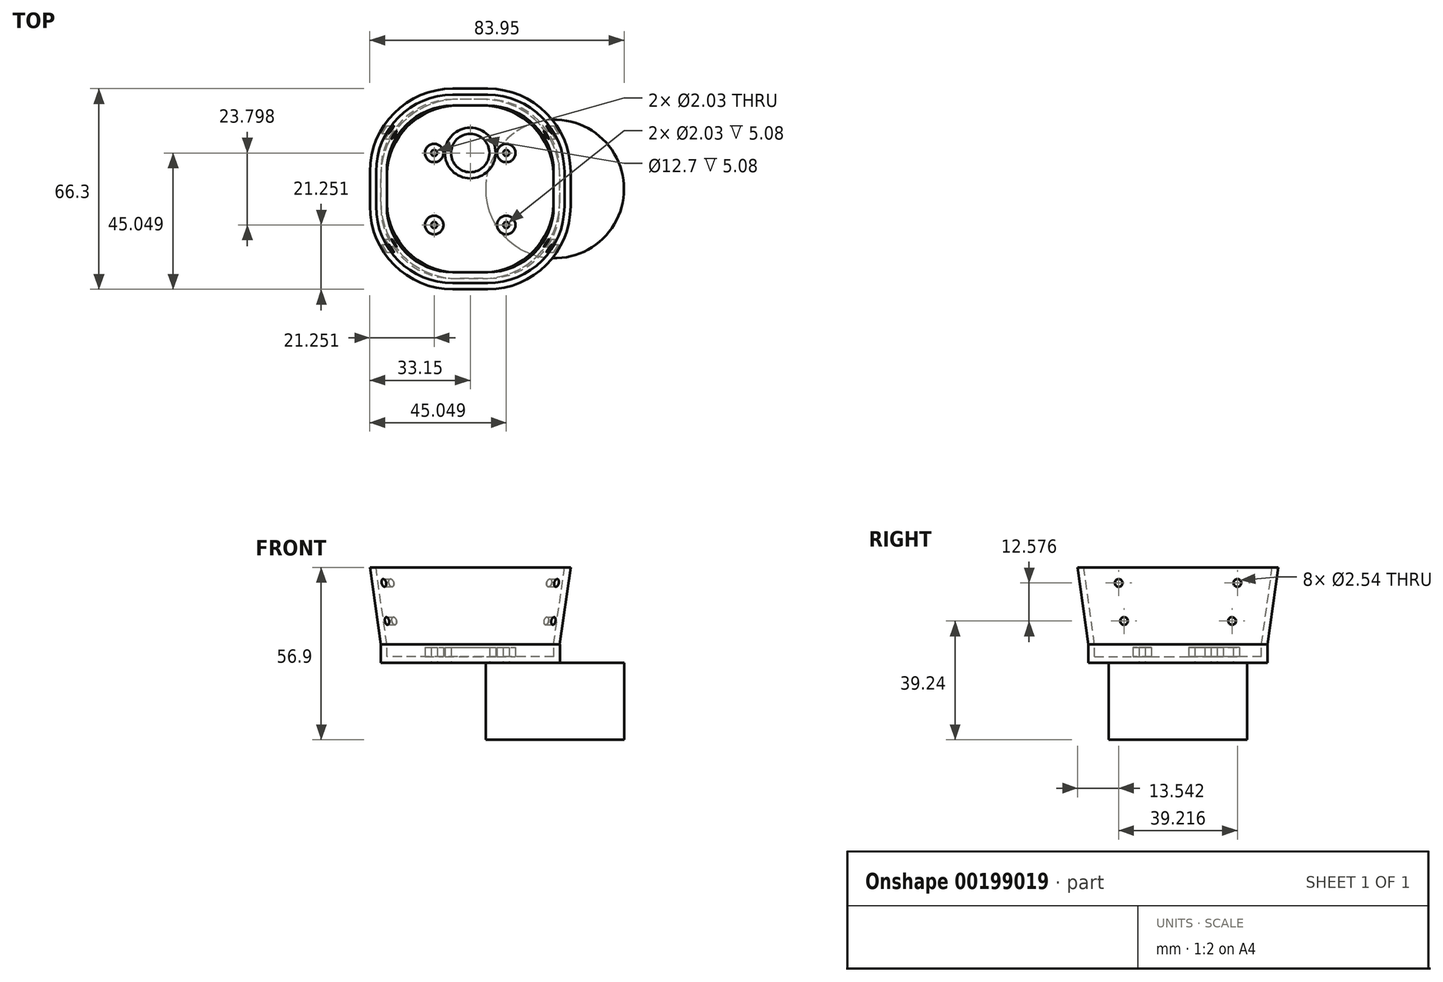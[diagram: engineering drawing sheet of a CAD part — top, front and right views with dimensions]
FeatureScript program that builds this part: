
annotation { "Feature Type Name" : "Feature", "Feature Type Description" : "" }
export const myFeature = defineFeature(function(context is Context, id is Id, definition is map)
    precondition{}
    {
        {
            var Q0;
            Q0=qCreatedBy(makeId("Top.planeOp"),FACE);
            var sketch = newSketch(context, id + "F0", { "sketchPlane" : qUnion([Q0])});
            skLineSegment(sketch, "E0.bottom", {"start": v(29.6, -29.6) * mm, "end": v(-29.6, -29.6) * mm});
            skLineSegment(sketch, "E0.top", {"start": v(29.6, 29.6) * mm, "end": v(-29.6, 29.6) * mm});
            skLineSegment(sketch, "E0.left", {"start": v(29.6, -29.6) * mm, "end": v(29.6, 29.6) * mm});
            skLineSegment(sketch, "E0.right", {"start": v(-29.6, -29.6) * mm, "end": v(-29.6, 29.6) * mm});
            skPoint(sketch, "E0.middle", {"position": v(0, 0) * mm});
            skSolve(sketch);
        }
        {
            var Q0;
            Q0 = qSketchRegion(id + "F0", true);
            extrude(context, id + "F1", {"entities" : qUnion([Q0]), "depth" : 1.02 * mm});
        }
        {
            var Q0;
            Q0=makeQuery(id+"F1.opExtrude","SWEPT_EDGE",EDGE,{"disambiguationData":[OSD([sQuery(id+"F0.wireOp",EDGE,"E0.top"),sQuery(id+"F0.wireOp",EDGE,"E0.right")])]});
            var Q1;
            Q1=makeQuery(id+"F1.opExtrude","SWEPT_EDGE",EDGE,{"disambiguationData":[OSD([sQuery(id+"F0.wireOp",EDGE,"E0.bottom"),sQuery(id+"F0.wireOp",EDGE,"E0.right")])]});
            var Q2;
            Q2=makeQuery(id+"F1.opExtrude","SWEPT_EDGE",EDGE,{"disambiguationData":[OSD([sQuery(id+"F0.wireOp",EDGE,"E0.bottom"),sQuery(id+"F0.wireOp",EDGE,"E0.left")])]});
            var Q3;
            Q3=makeQuery(id+"F1.opExtrude","SWEPT_EDGE",EDGE,{"disambiguationData":[OSD([sQuery(id+"F0.wireOp",EDGE,"E0.top"),sQuery(id+"F0.wireOp",EDGE,"E0.left")])]});
            fillet(context, id + "F2", {"entities" : qUnion([Q0, Q1, Q2, Q3]), "radius" : 25.4 * mm, "tangentPropagation" : true, "allowEdgeOverflow" : false});
        }
        {
            var Q0;
            Q0=makeQuery(id+"F1.opExtrude","CAP_FACE",FACE,{"disambiguationData":[OSD([sQuery(id+"F0.wireOp",EDGE,"E0.bottom"),sQuery(id+"F0.wireOp",EDGE,"E0.top"),sQuery(id+"F0.wireOp",EDGE,"E0.left"),sQuery(id+"F0.wireOp",EDGE,"E0.right")])],"isStart":false});
            var sketch = newSketch(context, id + "F3", { "sketchPlane" : qUnion([Q0])});
            skArc(sketch, "E1.0", {"start": v(-27.56, -4.2) * mm, "mid": v(-20.71, -20.71) * mm, "end": v(-4.2, -27.56) * mm});
            skLineSegment(sketch, "E1.1", {"start": v(-27.56, 4.2) * mm, "end": v(-27.56, -4.2) * mm});
            skLineSegment(sketch, "E1.2", {"start": v(-4.2, -27.56) * mm, "end": v(4.2, -27.56) * mm});
            skArc(sketch, "E1.3", {"start": v(-4.2, 27.56) * mm, "mid": v(-20.71, 20.71) * mm, "end": v(-27.56, 4.2) * mm});
            skArc(sketch, "E1.4", {"start": v(4.2, -27.56) * mm, "mid": v(20.71, -20.71) * mm, "end": v(27.56, -4.2) * mm});
            skLineSegment(sketch, "E1.5", {"start": v(27.56, -4.2) * mm, "end": v(27.56, 4.2) * mm});
            skArc(sketch, "E1.6", {"start": v(27.56, 4.2) * mm, "mid": v(20.71, 20.71) * mm, "end": v(4.2, 27.56) * mm});
            skLineSegment(sketch, "E1.7", {"start": v(4.2, 27.56) * mm, "end": v(-4.2, 27.56) * mm});
            skSolve(sketch);
        }
        {
            var Q0;
            Q0 = qSketchRegion(id + "F3", true);
            extrude(context, id + "F4", {"entities" : qUnion([Q0]), "operationType" : NewBodyOperationType.REMOVE, "oppositeDirection" : true, "depth" : 25.4 * mm});
        }
        {
            var Q0;
            Q0=makeQuery(id+"F1.opExtrude","CAP_FACE",FACE,{"disambiguationData":[OSD([sQuery(id+"F0.wireOp",EDGE,"E0.bottom"),sQuery(id+"F0.wireOp",EDGE,"E0.top"),sQuery(id+"F0.wireOp",EDGE,"E0.left"),sQuery(id+"F0.wireOp",EDGE,"E0.right")])],"isStart":true});
            var sketch = newSketch(context, id + "F5", { "sketchPlane" : qUnion([Q0])});
            skArc(sketch, "E2.0", {"start": v(-4.2, 29.6) * mm, "mid": v(-22.15, 22.15) * mm, "end": v(-29.6, 4.2) * mm});
            skLineSegment(sketch, "E2.1", {"start": v(4.2, 29.6) * mm, "end": v(-4.2, 29.6) * mm});
            skArc(sketch, "E2.2", {"start": v(29.6, 4.2) * mm, "mid": v(22.15, 22.15) * mm, "end": v(4.2, 29.6) * mm});
            skLineSegment(sketch, "E2.3", {"start": v(29.6, 4.2) * mm, "end": v(29.6, -4.2) * mm});
            skLineSegment(sketch, "E2.4", {"start": v(-29.6, 4.2) * mm, "end": v(-29.6, -4.2) * mm});
            skArc(sketch, "E2.5", {"start": v(-29.6, -4.2) * mm, "mid": v(-22.15, -22.15) * mm, "end": v(-4.2, -29.6) * mm});
            skLineSegment(sketch, "E2.6", {"start": v(4.2, -29.6) * mm, "end": v(-4.2, -29.6) * mm});
            skArc(sketch, "E2.7", {"start": v(4.2, -29.6) * mm, "mid": v(22.15, -22.15) * mm, "end": v(29.6, -4.2) * mm});
            skSolve(sketch);
        }
        {
            var Q0;
            Q0 = qSketchRegion(id + "F5", true);
            extrude(context, id + "F6", {"entities" : qUnion([Q0]), "operationType" : NewBodyOperationType.ADD, "depth" : 5.08 * mm});
        }
        {
            var Q0;
            Q0=makeQuery(id+"F6.opExtrude","CAP_FACE",FACE,{"disambiguationData":[OSD([sQuery(id+"F5.wireOp",EDGE,"E2.0"),sQuery(id+"F5.wireOp",EDGE,"E2.1"),sQuery(id+"F5.wireOp",EDGE,"E2.2"),sQuery(id+"F5.wireOp",EDGE,"E2.3"),sQuery(id+"F5.wireOp",EDGE,"E2.4"),sQuery(id+"F5.wireOp",EDGE,"E2.5"),sQuery(id+"F5.wireOp",EDGE,"E2.6"),sQuery(id+"F5.wireOp",EDGE,"E2.7")])],"isStart":false});
            var sketch = newSketch(context, id + "F7", { "sketchPlane" : qUnion([Q0])});
            skLineSegment(sketch, "E3", {"start": v(0, 0) * mm, "end": v(-4.77, 4.77) * mm, "construction": true});
            skCircle(sketch, "E4", {"center": v(-11.9, 11.9) * mm, "radius": 1.02 * mm});
            skCircle(sketch, "E5.MirrorC", {"center": v(-11.9, -11.9) * mm, "radius": 1.02 * mm});
            skCircle(sketch, "E6.MirrorC", {"center": v(11.9, 11.9) * mm, "radius": 1.02 * mm});
            skCircle(sketch, "E7.MirrorC", {"center": v(11.9, -11.9) * mm, "radius": 1.02 * mm});
            skLineSegment(sketch, "E8", {"start": v(-11.9, -11.9) * mm, "end": v(11.9, -11.9) * mm, "construction": true});
            skCircle(sketch, "E9", {"center": v(0, -11.9) * mm, "radius": 6.35 * mm});
            skSolve(sketch);
        }
        {
            var Q0;
            Q0 = qSketchRegion(id + "F7", true);
            extrude(context, id + "F8", {"entities" : qUnion([Q0]), "operationType" : NewBodyOperationType.REMOVE, "endBound" : BoundingType.UP_TO_NEXT, "oppositeDirection" : true, "depth" : 25.4 * mm});
        }
        {
            var Q0;
            Q0=makeQuery(id+"F1.opExtrude","CAP_FACE",FACE,{"disambiguationData":[OSD([sQuery(id+"F0.wireOp",EDGE,"E0.bottom"),sQuery(id+"F0.wireOp",EDGE,"E0.top"),sQuery(id+"F0.wireOp",EDGE,"E0.left"),sQuery(id+"F0.wireOp",EDGE,"E0.right")])],"isStart":false});
            var sketch = newSketch(context, id + "F9", { "sketchPlane" : qUnion([Q0])});
            skArc(sketch, "E10.0", {"start": v(-4.2, 29.6) * mm, "mid": v(-22.15, 22.15) * mm, "end": v(-29.6, 4.2) * mm});
            skLineSegment(sketch, "E10.1", {"start": v(-29.6, -4.2) * mm, "end": v(-29.6, 4.2) * mm});
            skLineSegment(sketch, "E10.2", {"start": v(4.2, 29.6) * mm, "end": v(-4.2, 29.6) * mm});
            skArc(sketch, "E10.3", {"start": v(29.6, 4.2) * mm, "mid": v(22.15, 22.15) * mm, "end": v(4.2, 29.6) * mm});
            skLineSegment(sketch, "E10.4", {"start": v(29.6, -4.2) * mm, "end": v(29.6, 4.2) * mm});
            skArc(sketch, "E10.5", {"start": v(4.2, -29.6) * mm, "mid": v(22.15, -22.15) * mm, "end": v(29.6, -4.2) * mm});
            skLineSegment(sketch, "E10.6", {"start": v(4.2, -29.6) * mm, "end": v(-4.2, -29.6) * mm});
            skArc(sketch, "E10.7", {"start": v(-29.6, -4.2) * mm, "mid": v(-22.15, -22.15) * mm, "end": v(-4.2, -29.6) * mm});
            skArc(sketch, "E10.8", {"start": v(-4.2, 27.56) * mm, "mid": v(-20.71, 20.71) * mm, "end": v(-27.56, 4.2) * mm});
            skLineSegment(sketch, "E10.9", {"start": v(4.2, 27.56) * mm, "end": v(-4.2, 27.56) * mm});
            skArc(sketch, "E10.10", {"start": v(27.56, 4.2) * mm, "mid": v(20.71, 20.71) * mm, "end": v(4.2, 27.56) * mm});
            skLineSegment(sketch, "E10.11", {"start": v(27.56, -4.2) * mm, "end": v(27.56, 4.2) * mm});
            skArc(sketch, "E10.12", {"start": v(4.2, -27.56) * mm, "mid": v(20.71, -20.71) * mm, "end": v(27.56, -4.2) * mm});
            skLineSegment(sketch, "E10.13", {"start": v(-4.2, -27.56) * mm, "end": v(4.2, -27.56) * mm});
            skArc(sketch, "E10.14", {"start": v(-27.56, -4.2) * mm, "mid": v(-20.71, -20.71) * mm, "end": v(-4.2, -27.56) * mm});
            skLineSegment(sketch, "E10.15", {"start": v(-27.56, 4.2) * mm, "end": v(-27.56, -4.2) * mm});
            skSolve(sketch);
        }
        {
            var Q0;
            Q0=makeQuery(id+"F6.opExtrude","CAP_FACE",FACE,{"disambiguationData":[OSD([sQuery(id+"F5.wireOp",EDGE,"E2.0"),sQuery(id+"F5.wireOp",EDGE,"E2.1"),sQuery(id+"F5.wireOp",EDGE,"E2.2"),sQuery(id+"F5.wireOp",EDGE,"E2.3"),sQuery(id+"F5.wireOp",EDGE,"E2.4"),sQuery(id+"F5.wireOp",EDGE,"E2.5"),sQuery(id+"F5.wireOp",EDGE,"E2.6"),sQuery(id+"F5.wireOp",EDGE,"E2.7")])],"isStart":true});
            shell(context, id + "F10", {"entities" : qUnion([Q0]), "thickness" : 2.03 * mm});
        }
        {
            var Q0;
            Q0=makeQuery(id+"F9.imprint","IMPRINT",FACE,{"disambiguationData":[TD([[makeQuery(id+"F9.imprint","IMPRINT",EDGE,{"derivedFrom":sQuery(id+"F9.wireOp",EDGE,"E10.0")}),1.0]])]});
            cPlane(context, id + "F11", {"entities" : qUnion([Q0]), "cplaneType" : CPlaneType.OFFSET, "offset" : 25.4 * mm, "width" : 152.4 * mm, "height" : 152.4 * mm});
        }
        {
            var Q0;
            Q0=qCreatedBy(id+"F11.planeOp",FACE);
            var sketch = newSketch(context, id + "F12", { "sketchPlane" : qUnion([Q0])});
            skLineSegment(sketch, "E11.bottom", {"start": v(5.72, -31.12) * mm, "end": v(-5.72, -31.12) * mm});
            skLineSegment(sketch, "E11.top", {"start": v(5.71, 31.12) * mm, "end": v(-5.72, 31.12) * mm});
            skLineSegment(sketch, "E11.left", {"start": v(31.12, -5.72) * mm, "end": v(31.12, 5.71) * mm});
            skLineSegment(sketch, "E11.right", {"start": v(-31.12, -5.71) * mm, "end": v(-31.12, 5.72) * mm});
            skPoint(sketch, "E11.middle", {"position": v(0, 0) * mm});
            skPoint(sketch, "E12.visualSharp", {"position": v(-31.12, 31.12) * mm});
            skArc(sketch, "E12.filletArc", {"start": v(-5.72, 31.12) * mm, "mid": v(-23.68, 23.68) * mm, "end": v(-31.12, 5.72) * mm});
            skPoint(sketch, "E13.visualSharp", {"position": v(31.11, 31.12) * mm});
            skArc(sketch, "E13.filletArc", {"start": v(31.11, 5.71) * mm, "mid": v(23.68, 23.68) * mm, "end": v(5.71, 31.12) * mm});
            skPoint(sketch, "E14.visualSharp", {"position": v(31.12, -31.12) * mm});
            skArc(sketch, "E14.filletArc", {"start": v(5.72, -31.12) * mm, "mid": v(23.68, -23.68) * mm, "end": v(31.11, -5.72) * mm});
            skPoint(sketch, "E15.visualSharp", {"position": v(-31.12, -31.12) * mm});
            skArc(sketch, "E15.filletArc", {"start": v(-31.12, -5.72) * mm, "mid": v(-23.68, -23.68) * mm, "end": v(-5.71, -31.12) * mm});
            skLineSegment(sketch, "E16.0", {"start": v(5.71, 33.15) * mm, "end": v(-5.72, 33.15) * mm});
            skArc(sketch, "E16.1", {"start": v(33.15, 5.71) * mm, "mid": v(25.11, 25.11) * mm, "end": v(5.71, 33.15) * mm});
            skArc(sketch, "E16.2", {"start": v(-5.72, 33.15) * mm, "mid": v(-25.11, 25.11) * mm, "end": v(-33.15, 5.72) * mm});
            skLineSegment(sketch, "E16.3", {"start": v(33.15, -5.72) * mm, "end": v(33.15, 5.71) * mm});
            skLineSegment(sketch, "E16.4", {"start": v(-33.15, -5.72) * mm, "end": v(-33.15, 5.72) * mm});
            skArc(sketch, "E16.5", {"start": v(-33.15, -5.72) * mm, "mid": v(-25.11, -25.11) * mm, "end": v(-5.72, -33.15) * mm});
            skLineSegment(sketch, "E16.6", {"start": v(5.72, -33.15) * mm, "end": v(-5.72, -33.15) * mm});
            skArc(sketch, "E16.7", {"start": v(5.72, -33.15) * mm, "mid": v(25.11, -25.11) * mm, "end": v(33.15, -5.72) * mm});
            skSolve(sketch);
        }
        {
            var Q0;
            Q0=qCreatedBy(id+"F11.planeOp",FACE);
            var sketch = newSketch(context, id + "F13", { "sketchPlane" : qUnion([Q0])});
            skArc(sketch, "E17.0", {"start": v(33.15, 5.71) * mm, "mid": v(25.11, 25.11) * mm, "end": v(5.71, 33.15) * mm});
            skLineSegment(sketch, "E17.1", {"start": v(5.71, 33.15) * mm, "end": v(-5.72, 33.15) * mm});
            skArc(sketch, "E17.2", {"start": v(-5.72, 33.15) * mm, "mid": v(-25.11, 25.11) * mm, "end": v(-33.15, 5.72) * mm});
            skLineSegment(sketch, "E17.3", {"start": v(-33.15, -5.72) * mm, "end": v(-33.15, 5.72) * mm});
            skArc(sketch, "E17.4", {"start": v(-33.15, -5.72) * mm, "mid": v(-25.11, -25.11) * mm, "end": v(-5.72, -33.15) * mm});
            skLineSegment(sketch, "E17.5", {"start": v(5.72, -33.15) * mm, "end": v(-5.72, -33.15) * mm});
            skArc(sketch, "E17.6", {"start": v(5.72, -33.15) * mm, "mid": v(25.11, -25.11) * mm, "end": v(33.15, -5.72) * mm});
            skLineSegment(sketch, "E17.7", {"start": v(33.15, -5.72) * mm, "end": v(33.15, 5.71) * mm});
            skSolve(sketch);
        }
        {
            var Q0;
            Q0 = qSketchRegion(id + "F13", true);
            extrude(context, id + "F14", {"entities" : qUnion([Q0]), "operationType" : NewBodyOperationType.ADD, "oppositeDirection" : true, "depth" : 25.4 * mm, "hasDraft" : true, "draftAngle" : 8 * degree, "draftPullDirection" : true});
        }
        {
            var Q0;
            Q0=makeQuery(id+"F12.imprint","IMPRINT",FACE,{"disambiguationData":[TD([[makeQuery(id+"F12.imprint","IMPRINT",EDGE,{"derivedFrom":sQuery(id+"F12.wireOp",EDGE,"E11.bottom")}),-1.0]])]});
            var sketch = newSketch(context, id + "F15", { "sketchPlane" : qUnion([Q0])});
            skArc(sketch, "E18.0", {"start": v(-5.72, 31.12) * mm, "mid": v(-23.68, 23.68) * mm, "end": v(-31.12, 5.72) * mm});
            skLineSegment(sketch, "E18.1", {"start": v(-31.12, -5.71) * mm, "end": v(-31.12, 5.72) * mm});
            skArc(sketch, "E18.2", {"start": v(-31.12, -5.72) * mm, "mid": v(-23.68, -23.68) * mm, "end": v(-5.71, -31.12) * mm});
            skLineSegment(sketch, "E18.3", {"start": v(5.72, -31.12) * mm, "end": v(-5.72, -31.12) * mm});
            skArc(sketch, "E18.4", {"start": v(5.72, -31.12) * mm, "mid": v(23.68, -23.68) * mm, "end": v(31.11, -5.72) * mm});
            skLineSegment(sketch, "E18.5", {"start": v(31.12, -5.72) * mm, "end": v(31.12, 5.71) * mm});
            skArc(sketch, "E18.6", {"start": v(31.11, 5.71) * mm, "mid": v(23.68, 23.68) * mm, "end": v(5.71, 31.12) * mm});
            skLineSegment(sketch, "E18.7", {"start": v(5.71, 31.12) * mm, "end": v(-5.72, 31.12) * mm});
            skSolve(sketch);
        }
        {
            var Q0;
            Q0 = qSketchRegion(id + "F15", true);
            extrude(context, id + "F16", {"entities" : qUnion([Q0]), "operationType" : NewBodyOperationType.REMOVE, "oppositeDirection" : true, "depth" : 25.4 * mm, "hasDraft" : true, "draftAngle" : 8 * degree, "draftPullDirection" : true});
        }
        {
            var Q0;
            Q0=qCreatedBy(makeId("Right.planeOp"),FACE);
            var sketch = newSketch(context, id + "F17", { "sketchPlane" : qUnion([Q0])});
            skCircle(sketch, "E19", {"center": v(-19.6, 21.34) * mm, "radius": 1.27 * mm});
            skCircle(sketch, "E20", {"center": v(-17.84, 8.76) * mm, "radius": 1.27 * mm});
            skCircle(sketch, "E21.MirrorC", {"center": v(19.6, 21.34) * mm, "radius": 1.27 * mm});
            skCircle(sketch, "E22.MirrorC", {"center": v(17.84, 8.76) * mm, "radius": 1.27 * mm});
            skSolve(sketch);
        }
        {
            var Q0;
            Q0 = qSketchRegion(id + "F17", true);
            extrude(context, id + "F18", {"entities" : qUnion([Q0]), "operationType" : NewBodyOperationType.REMOVE, "endBound" : BoundingType.THROUGH_ALL, "oppositeDirection" : true, "depth" : 25.4 * mm, "hasSecondDirection" : true, "secondDirectionBound" : SecondDirectionBoundingType.THROUGH_ALL, "secondDirectionOppositeDirection" : false, "secondDirectionDepth" : 25.4 * mm});
        }
        {
            var Q0;
            Q0=makeQuery(id+"F6.opExtrude","CAP_FACE",FACE,{"disambiguationData":[OSD([sQuery(id+"F5.wireOp",EDGE,"E2.0"),sQuery(id+"F5.wireOp",EDGE,"E2.1"),sQuery(id+"F5.wireOp",EDGE,"E2.2"),sQuery(id+"F5.wireOp",EDGE,"E2.3"),sQuery(id+"F5.wireOp",EDGE,"E2.4"),sQuery(id+"F5.wireOp",EDGE,"E2.5"),sQuery(id+"F5.wireOp",EDGE,"E2.6"),sQuery(id+"F5.wireOp",EDGE,"E2.7")])],"isStart":false});
            var sketch = newSketch(context, id + "F19", { "sketchPlane" : qUnion([Q0])});
            skCircle(sketch, "E23", {"center": v(27.94, 0) * mm, "radius": 22.86 * mm});
            skSolve(sketch);
        }
        {
            var Q0;
            Q0 = qSketchRegion(id + "F19", true);
            extrude(context, id + "F20", {"entities" : qUnion([Q0]), "operationType" : NewBodyOperationType.ADD, "depth" : 25.4 * mm, "offsetDistance" : 25.4 * mm});
        }
    });
